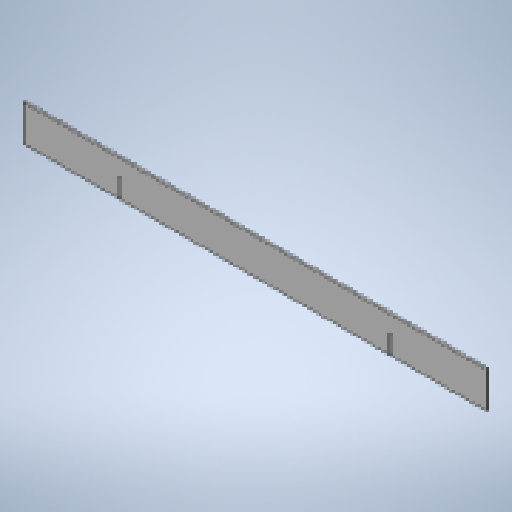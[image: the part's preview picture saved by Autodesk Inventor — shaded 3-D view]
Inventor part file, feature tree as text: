
AUTODESK INVENTOR PART (.ipt)
format: ipt  version: 2025 (Build 290162010, 162A)  size: 193,024 bytes
history: native  units: mm
features: sketch x3, extrude x2, sheet_metal_op x1, other x1, projected_geometry x1
ambient origin geometry x8: Origin, YZ Plane, XZ Plane, XY Plane, X Axis, Y Axis, Z Axis, Center Point
bodies: Body1 (feature_tree)
feature tree (8):
  sheet_metal_op  "Face1"
  extrude  "Extrusion1"  Depth=50.0mm
  extrude  "Extrusion2"  Depth=3.0mm
  sketch  "Sketch2"  dims[d18=750.0mm d19=50.0mm]
  other  "Plate2"
  sketch  "Sketch3"  dims[d20=45.0mm d21=3.0mm]
  sketch  "Sketch4"  dims[d23=3.0mm d24=26.0mm d25=0.0mm d26=0.0mm d30=190.0mm d31=190.0mm d32=3.0mm d33=26.0mm d35=60.0mm d36=60.0mm d37=0.0mm d38=0.0mm]
  projected_geometry  "Projected Loop1"
